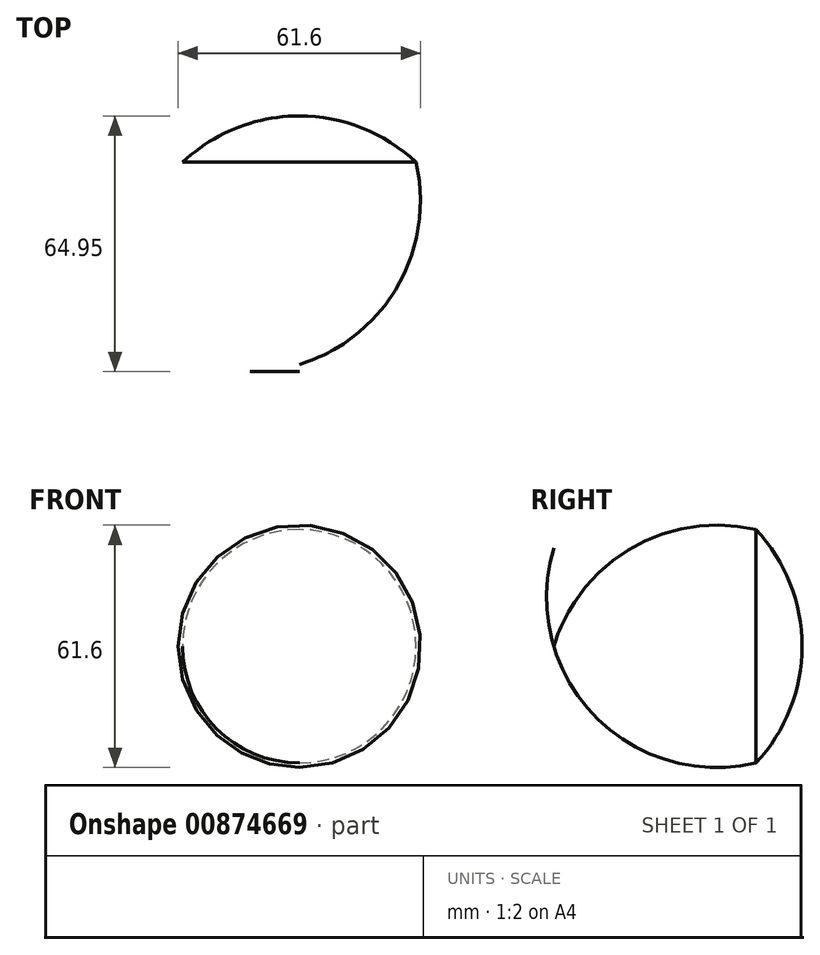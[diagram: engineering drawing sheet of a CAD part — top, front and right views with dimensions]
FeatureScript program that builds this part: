
annotation { "Feature Type Name" : "Feature", "Feature Type Description" : "" }
export const myFeature = defineFeature(function(context is Context, id is Id, definition is map)
    precondition{}
    {
        {
            var Q0;
            Q0=qCreatedBy(makeId("Top.planeOp"),FACE);
            var sketch = newSketch(context, id + "F0", { "sketchPlane" : qUnion([Q0])});
            skLineSegment(sketch, "E0.bottom", {"start": v(0, 0) * mm, "end": v(25, 0) * mm, "construction": true});
            skLineSegment(sketch, "E0.top", {"start": v(0, 43.3) * mm, "end": v(25, 43.3) * mm, "construction": true});
            skLineSegment(sketch, "E0.left", {"start": v(0, 0) * mm, "end": v(0, 43.3) * mm, "construction": true});
            skLineSegment(sketch, "E0.right", {"start": v(25, 0) * mm, "end": v(25, 43.3) * mm, "construction": true});
            skLineSegment(sketch, "E1", {"start": v(0, 43.3) * mm, "end": v(25, 0) * mm});
            skLineSegment(sketch, "E2", {"start": v(25, 0) * mm, "end": v(-25, 0) * mm});
            skLineSegment(sketch, "E3", {"start": v(-25, 0) * mm, "end": v(0, 43.3) * mm});
            skCircle(sketch, "E4", {"center": v(-12.5, 21.65) * mm, "radius": 43.3 * mm});
            skCircle(sketch, "E5", {"center": v(12.5, 21.65) * mm, "radius": 43.3 * mm});
            skCircle(sketch, "E6", {"center": v(0, 0) * mm, "radius": 43.3 * mm});
            skLineSegment(sketch, "E7", {"start": v(0, 43.3) * mm, "end": v(0, -19.8) * mm});
            skSolve(sketch);
        }
        {
            var Q0;
            {var subQ1=sQuery(id+"F0.wireOp",EDGE,"E2");var subQ3=sQuery(id+"F0.wireOp",EDGE,"E7");var subQ4=makeQuery(id+"F0.imprint","INTERSECT",VERTEX,{"derivedFrom":[subQ1,subQ3]});Q0=makeQuery(id+"F0.imprint","IMPRINT",FACE,{"disambiguationData":[TD([[makeQuery(id+"F0.imprint","IMPRINT",EDGE,{"disambiguationData":[TD([[subQ4,-1.0]])],"derivedFrom":subQ1}),1.0]])]});}
            var Q1;
            {var subQ0=sQuery(id+"F0.wireOp",EDGE,"E3");Q1=makeQuery(id+"F0.imprint","IMPRINT",FACE,{"disambiguationData":[TD([[makeQuery(id+"F0.imprint","IMPRINT",EDGE,{"derivedFrom":subQ0}),-1.0]])]});}
            var Q2;
            {var subQ0=sQuery(id+"F0.wireOp",EDGE,"E3");Q2=makeQuery(id+"F0.imprint","IMPRINT",FACE,{"disambiguationData":[TD([[makeQuery(id+"F0.imprint","IMPRINT",EDGE,{"derivedFrom":subQ0}),1.0]])]});}
            var Q3;
            Q3=sQuery(id+"F0.wireOp",EDGE,"E7");
            revolve(context, id + "F1", {"surfaceOperationType" : NewSurfaceOperationType.NEW, "entities" : qUnion([Q0, Q1, Q2]), "axis" : qUnion([Q3]), "revolveType" : RevolveType.FULL});
        }
    });
